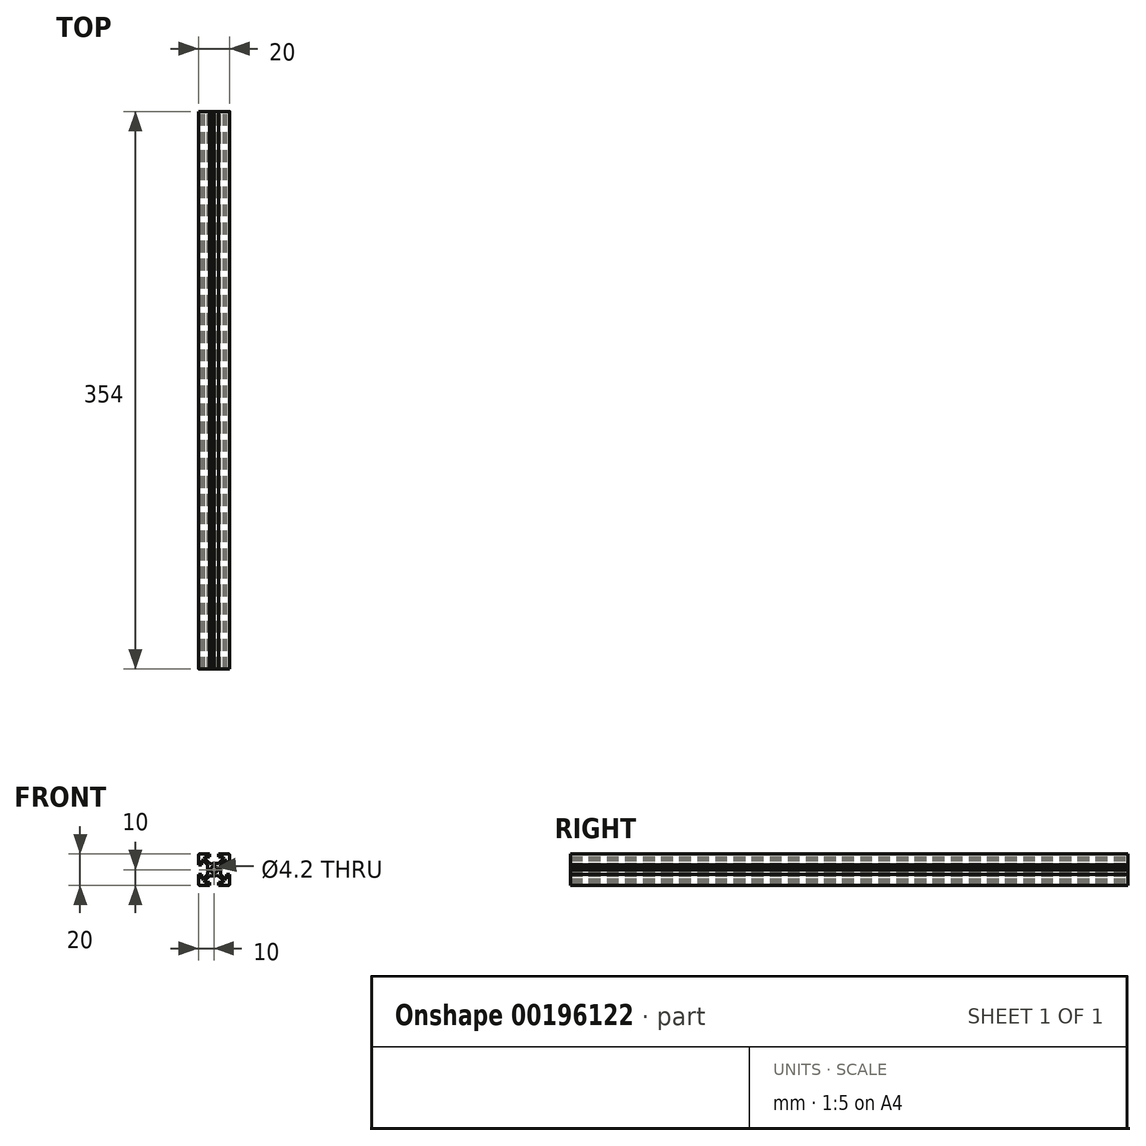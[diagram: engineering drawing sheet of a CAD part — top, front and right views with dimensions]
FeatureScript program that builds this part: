
annotation { "Feature Type Name" : "Feature", "Feature Type Description" : "" }
export const myFeature = defineFeature(function(context is Context, id is Id, definition is map)
    precondition{}
    {
        {
            var Q0;
            Q0=qCreatedBy(makeId("Front.planeOp"),FACE);
            var sketch = newSketch(context, id + "F0", { "sketchPlane" : qUnion([Q0])});
            skLineSegment(sketch, "E0.0", {"start": v(-6, -7.06) * mm, "end": v(-2.94, -4) * mm});
            skArc(sketch, "E0.1", {"start": v(-9, 10) * mm, "mid": v(-9.7, 9.7) * mm, "end": v(-10, 9) * mm});
            skLineSegment(sketch, "E0.2", {"start": v(6, 7.06) * mm, "end": v(2.94, 4) * mm});
            skLineSegment(sketch, "E0.3", {"start": v(4, 2.94) * mm, "end": v(7.06, 6) * mm});
            skCircle(sketch, "E0.4", {"center": v(0, 0) * mm, "radius": 2.1 * mm});
            skArc(sketch, "E0.5", {"start": v(9, -10) * mm, "mid": v(9.7, -9.7) * mm, "end": v(10, -9) * mm});
            skLineSegment(sketch, "E0.6", {"start": v(-4, -2.94) * mm, "end": v(-7.06, -6) * mm});
            skLineSegment(sketch, "E0.7", {"start": v(7.06, 6) * mm, "end": v(8, 6) * mm});
            skLineSegment(sketch, "E0.8", {"start": v(3, -10) * mm, "end": v(9, -10) * mm});
            skLineSegment(sketch, "E0.9", {"start": v(7.06, -6) * mm, "end": v(4, -2.94) * mm});
            skLineSegment(sketch, "E0.10", {"start": v(2.94, -4) * mm, "end": v(6, -7.06) * mm});
            skLineSegment(sketch, "E0.12", {"start": v(-3, 8) * mm, "end": v(-3, 10) * mm});
            skLineSegment(sketch, "E0.13", {"start": v(1.22, -3.75) * mm, "end": v(2.5, -4) * mm});
            skLineSegment(sketch, "E0.14", {"start": v(-9, -10) * mm, "end": v(-3, -10) * mm});
            skLineSegment(sketch, "E0.15", {"start": v(-0.9, 3.93) * mm, "end": v(-1.22, 3.75) * mm});
            skLineSegment(sketch, "E0.16", {"start": v(8, -6) * mm, "end": v(7.06, -6) * mm});
            skCircle(sketch, "E0.17", {"center": v(0, 0) * mm, "radius": 2.1 * mm});
            skLineSegment(sketch, "E0.18", {"start": v(9, 10) * mm, "end": v(3, 10) * mm});
            skLineSegment(sketch, "E0.19", {"start": v(8, -3) * mm, "end": v(8, -6) * mm});
            skLineSegment(sketch, "E0.20", {"start": v(8, 3) * mm, "end": v(10, 3) * mm});
            skLineSegment(sketch, "E0.21", {"start": v(-4, 2.94) * mm, "end": v(-4, 0.65) * mm});
            skArc(sketch, "E0.22", {"start": v(10, 9) * mm, "mid": v(9.7, 9.7) * mm, "end": v(9, 10) * mm});
            skLineSegment(sketch, "E0.23", {"start": v(-10, 9) * mm, "end": v(-10, 3) * mm});
            skLineSegment(sketch, "E0.24", {"start": v(-3.7, 0) * mm, "end": v(-3.93, -0.4) * mm});
            skLineSegment(sketch, "E0.25", {"start": v(0.4, 3.93) * mm, "end": v(0, 3.7) * mm});
            skLineSegment(sketch, "E0.26", {"start": v(-3, 10) * mm, "end": v(-9, 10) * mm});
            skLineSegment(sketch, "E0.27", {"start": v(-3.93, 0.4) * mm, "end": v(-3.7, 0) * mm});
            skLineSegment(sketch, "E0.29", {"start": v(-6, -7.06) * mm, "end": v(-2.94, -4) * mm});
            skLineSegment(sketch, "E0.30", {"start": v(-7.06, 6) * mm, "end": v(-4, 2.94) * mm});
            skArc(sketch, "E0.31", {"start": v(-9, 10) * mm, "mid": v(-9.7, 9.7) * mm, "end": v(-10, 9) * mm});
            skLineSegment(sketch, "E0.32", {"start": v(-6, 7.06) * mm, "end": v(-6, 8) * mm});
            skLineSegment(sketch, "E0.33", {"start": v(-3.93, -0.9) * mm, "end": v(-3.75, -1.22) * mm});
            skLineSegment(sketch, "E0.34", {"start": v(4, -2.94) * mm, "end": v(4, -0.65) * mm});
            skLineSegment(sketch, "E0.36", {"start": v(6, 8) * mm, "end": v(6, 7.06) * mm});
            skLineSegment(sketch, "E0.37", {"start": v(4, 2.5) * mm, "end": v(4, 2.94) * mm});
            skLineSegment(sketch, "E0.38", {"start": v(3.7, 0) * mm, "end": v(3.93, 0.4) * mm});
            skArc(sketch, "E0.39", {"start": v(-4, 0.65) * mm, "mid": v(-3.98, 0.52) * mm, "end": v(-3.93, 0.4) * mm});
            skLineSegment(sketch, "E0.40", {"start": v(3.93, 0.9) * mm, "end": v(3.75, 1.22) * mm});
            skLineSegment(sketch, "E0.41", {"start": v(2.94, 4) * mm, "end": v(0.65, 4) * mm});
            skArc(sketch, "E0.42", {"start": v(-3.93, -0.4) * mm, "mid": v(-4, -0.65) * mm, "end": v(-3.93, -0.9) * mm});
            skLineSegment(sketch, "E0.43", {"start": v(-2.94, 4) * mm, "end": v(-6, 7.06) * mm});
            skLineSegment(sketch, "E0.44", {"start": v(10, 3) * mm, "end": v(10, 9) * mm});
            skLineSegment(sketch, "E0.45", {"start": v(-3.75, -1.22) * mm, "end": v(-4, -2.5) * mm});
            skArc(sketch, "E0.46", {"start": v(3.93, 0.4) * mm, "mid": v(4, 0.65) * mm, "end": v(3.93, 0.9) * mm});
            skLineSegment(sketch, "E0.48", {"start": v(-8, -3) * mm, "end": v(-10, -3) * mm});
            skLineSegment(sketch, "E0.49", {"start": v(-10, -3) * mm, "end": v(-10, -9) * mm});
            skLineSegment(sketch, "E0.50", {"start": v(0, 3.7) * mm, "end": v(-0.4, 3.93) * mm});
            skLineSegment(sketch, "E0.51", {"start": v(6, -8) * mm, "end": v(3, -8) * mm});
            skLineSegment(sketch, "E0.52", {"start": v(-2.5, 4) * mm, "end": v(-2.94, 4) * mm});
            skLineSegment(sketch, "E0.53", {"start": v(-2.94, -4) * mm, "end": v(-0.65, -4) * mm});
            skLineSegment(sketch, "E0.54", {"start": v(-6, 8) * mm, "end": v(-3, 8) * mm});
            skLineSegment(sketch, "E0.55", {"start": v(-7.06, -6) * mm, "end": v(-8, -6) * mm});
            skLineSegment(sketch, "E0.56", {"start": v(3, 8) * mm, "end": v(6, 8) * mm});
            skLineSegment(sketch, "E0.57", {"start": v(-3, -8) * mm, "end": v(-6, -8) * mm});
            skLineSegment(sketch, "E0.58", {"start": v(8, 6) * mm, "end": v(8, 3) * mm});
            skArc(sketch, "E0.59", {"start": v(0.65, 4) * mm, "mid": v(0.52, 3.98) * mm, "end": v(0.4, 3.93) * mm});
            skLineSegment(sketch, "E0.60", {"start": v(-8, -6) * mm, "end": v(-8, -3) * mm});
            skLineSegment(sketch, "E0.61", {"start": v(2.5, -4) * mm, "end": v(2.94, -4) * mm});
            skLineSegment(sketch, "E0.62", {"start": v(-4, -2.94) * mm, "end": v(-7.06, -6) * mm});
            skLineSegment(sketch, "E0.63", {"start": v(-8, 6) * mm, "end": v(-7.06, 6) * mm});
            skArc(sketch, "E0.64", {"start": v(-0.4, 3.93) * mm, "mid": v(-0.65, 4) * mm, "end": v(-0.9, 3.93) * mm});
            skLineSegment(sketch, "E0.65", {"start": v(4, 2.94) * mm, "end": v(7.06, 6) * mm});
            skLineSegment(sketch, "E0.66", {"start": v(3, 10) * mm, "end": v(3, 8) * mm});
            skLineSegment(sketch, "E0.67", {"start": v(6, 7.06) * mm, "end": v(2.94, 4) * mm});
            skLineSegment(sketch, "E0.68", {"start": v(3.75, 1.22) * mm, "end": v(4, 2.5) * mm});
            skArc(sketch, "E0.70", {"start": v(-10, -9) * mm, "mid": v(-9.7, -9.7) * mm, "end": v(-9, -10) * mm});
            skArc(sketch, "E0.71", {"start": v(9, -10) * mm, "mid": v(9.7, -9.7) * mm, "end": v(10, -9) * mm});
            skLineSegment(sketch, "E0.72", {"start": v(-1.22, 3.75) * mm, "end": v(-2.5, 4) * mm});
            skLineSegment(sketch, "E0.73", {"start": v(-10, 3) * mm, "end": v(-8, 3) * mm});
            skLineSegment(sketch, "E0.74", {"start": v(-4, -2.5) * mm, "end": v(-4, -2.94) * mm});
            skLineSegment(sketch, "E0.79", {"start": v(3.93, -0.4) * mm, "end": v(3.7, 0) * mm});
            skLineSegment(sketch, "E0.81", {"start": v(-10, 3) * mm, "end": v(-8, 3) * mm});
            skLineSegment(sketch, "E0.82", {"start": v(-6, 8) * mm, "end": v(-3, 8) * mm});
            skLineSegment(sketch, "E0.86", {"start": v(2.5, -4) * mm, "end": v(2.94, -4) * mm});
            skLineSegment(sketch, "E0.88", {"start": v(-3.75, -1.22) * mm, "end": v(-4, -2.5) * mm});
            skLineSegment(sketch, "E0.89", {"start": v(3.75, 1.22) * mm, "end": v(4, 2.5) * mm});
            skLineSegment(sketch, "E0.90", {"start": v(-3, 8) * mm, "end": v(-3, 10) * mm});
            skLineSegment(sketch, "E0.91", {"start": v(-7.06, 6) * mm, "end": v(-4, 2.94) * mm});
            skLineSegment(sketch, "E0.93", {"start": v(8, -3) * mm, "end": v(8, -6) * mm});
            skLineSegment(sketch, "E0.100", {"start": v(-8, -6) * mm, "end": v(-8, -3) * mm});
            skLineSegment(sketch, "E0.101", {"start": v(-8, -3) * mm, "end": v(-10, -3) * mm});
            skLineSegment(sketch, "E0.102", {"start": v(0, -3.7) * mm, "end": v(0.4, -3.93) * mm});
            skLineSegment(sketch, "E0.106", {"start": v(8, -6) * mm, "end": v(7.06, -6) * mm});
            skLineSegment(sketch, "E0.109", {"start": v(2.94, 4) * mm, "end": v(0.65, 4) * mm});
            skLineSegment(sketch, "E0.110", {"start": v(10, 3) * mm, "end": v(10, 9) * mm});
            skArc(sketch, "E0.111", {"start": v(0.4, -3.93) * mm, "mid": v(0.65, -4) * mm, "end": v(0.9, -3.93) * mm});
            skLineSegment(sketch, "E0.113", {"start": v(6, 8) * mm, "end": v(6, 7.06) * mm});
            skLineSegment(sketch, "E0.114", {"start": v(-3, -8) * mm, "end": v(-6, -8) * mm});
            skLineSegment(sketch, "E0.116", {"start": v(-6, -8) * mm, "end": v(-6, -7.06) * mm});
            skLineSegment(sketch, "E0.117", {"start": v(4, -2.94) * mm, "end": v(4, -0.65) * mm});
            skArc(sketch, "E0.119", {"start": v(-10, -9) * mm, "mid": v(-9.7, -9.7) * mm, "end": v(-9, -10) * mm});
            skLineSegment(sketch, "E0.120", {"start": v(-2.5, 4) * mm, "end": v(-2.94, 4) * mm});
            skLineSegment(sketch, "E0.123", {"start": v(-10, 9) * mm, "end": v(-10, 3) * mm});
            skArc(sketch, "E0.124", {"start": v(-0.65, -4) * mm, "mid": v(-0.52, -3.98) * mm, "end": v(-0.4, -3.93) * mm});
            skLineSegment(sketch, "E0.125", {"start": v(-6, 7.06) * mm, "end": v(-6, 8) * mm});
            skLineSegment(sketch, "E0.126", {"start": v(10, -3) * mm, "end": v(8, -3) * mm});
            skLineSegment(sketch, "E0.129", {"start": v(9, 10) * mm, "end": v(3, 10) * mm});
            skLineSegment(sketch, "E0.131", {"start": v(-0.4, -3.93) * mm, "end": v(0, -3.7) * mm});
            skLineSegment(sketch, "E0.132", {"start": v(10, -9) * mm, "end": v(10, -3) * mm});
            skLineSegment(sketch, "E0.134", {"start": v(3, 8) * mm, "end": v(6, 8) * mm});
            skLineSegment(sketch, "E0.136", {"start": v(-4, 2.94) * mm, "end": v(-4, 0.65) * mm});
            skLineSegment(sketch, "E0.137", {"start": v(0, 3.7) * mm, "end": v(-0.4, 3.93) * mm});
            skArc(sketch, "E0.138", {"start": v(-3.93, -0.4) * mm, "mid": v(-4, -0.65) * mm, "end": v(-3.93, -0.9) * mm});
            skArc(sketch, "E0.140", {"start": v(4, -0.65) * mm, "mid": v(3.98, -0.52) * mm, "end": v(3.93, -0.4) * mm});
            skLineSegment(sketch, "E0.142", {"start": v(3, 10) * mm, "end": v(3, 8) * mm});
            skLineSegment(sketch, "E0.143", {"start": v(-7.06, -6) * mm, "end": v(-8, -6) * mm});
            skLineSegment(sketch, "E0.144", {"start": v(-3, -10) * mm, "end": v(-3, -8) * mm});
            skLineSegment(sketch, "E0.146", {"start": v(-3.93, 0.4) * mm, "end": v(-3.7, 0) * mm});
            skLineSegment(sketch, "E0.147", {"start": v(-8, 3) * mm, "end": v(-8, 6) * mm});
            skLineSegment(sketch, "E0.148", {"start": v(4, 2.5) * mm, "end": v(4, 2.94) * mm});
            skArc(sketch, "E0.149", {"start": v(3.93, 0.4) * mm, "mid": v(4, 0.65) * mm, "end": v(3.93, 0.9) * mm});
            skLineSegment(sketch, "E0.150", {"start": v(2.94, -4) * mm, "end": v(6, -7.06) * mm});
            skLineSegment(sketch, "E0.151", {"start": v(-10, -3) * mm, "end": v(-10, -9) * mm});
            skLineSegment(sketch, "E0.152", {"start": v(-4, -2.5) * mm, "end": v(-4, -2.94) * mm});
            skLineSegment(sketch, "E0.155", {"start": v(-9, -10) * mm, "end": v(-3, -10) * mm});
            skLineSegment(sketch, "E0.156", {"start": v(-2.94, -4) * mm, "end": v(-0.65, -4) * mm});
            skLineSegment(sketch, "E0.157", {"start": v(3, -10) * mm, "end": v(9, -10) * mm});
            skLineSegment(sketch, "E0.158", {"start": v(3, -8) * mm, "end": v(3, -10) * mm});
            skLineSegment(sketch, "E0.159", {"start": v(7.06, 6) * mm, "end": v(8, 6) * mm});
            skLineSegment(sketch, "E0.160", {"start": v(8, 6) * mm, "end": v(8, 3) * mm});
            skLineSegment(sketch, "E0.161", {"start": v(6, -8) * mm, "end": v(3, -8) * mm});
            skLineSegment(sketch, "E0.162", {"start": v(-2.94, 4) * mm, "end": v(-6, 7.06) * mm});
            skLineSegment(sketch, "E0.163", {"start": v(1.22, -3.75) * mm, "end": v(2.5, -4) * mm});
            skLineSegment(sketch, "E0.164", {"start": v(-3, 10) * mm, "end": v(-9, 10) * mm});
            skLineSegment(sketch, "E0.167", {"start": v(-1.22, 3.75) * mm, "end": v(-2.5, 4) * mm});
            skLineSegment(sketch, "E0.168", {"start": v(-8, 6) * mm, "end": v(-7.06, 6) * mm});
            skLineSegment(sketch, "E0.172", {"start": v(0.9, -3.93) * mm, "end": v(1.22, -3.75) * mm});
            skArc(sketch, "E0.173", {"start": v(0.65, 4) * mm, "mid": v(0.52, 3.98) * mm, "end": v(0.4, 3.93) * mm});
            skLineSegment(sketch, "E0.178", {"start": v(8, 3) * mm, "end": v(10, 3) * mm});
            skArc(sketch, "E0.183", {"start": v(10, 9) * mm, "mid": v(9.7, 9.7) * mm, "end": v(9, 10) * mm});
            skLineSegment(sketch, "E0.184", {"start": v(7.06, -6) * mm, "end": v(4, -2.94) * mm});
            skArc(sketch, "E0.185", {"start": v(-0.4, 3.93) * mm, "mid": v(-0.65, 4) * mm, "end": v(-0.9, 3.93) * mm});
            skLineSegment(sketch, "E0.188", {"start": v(6, -7.06) * mm, "end": v(6, -8) * mm});
            skLineSegment(sketch, "E0.190", {"start": v(-0.4, -3.93) * mm, "end": v(0, -3.7) * mm});
            skLineSegment(sketch, "E0.191", {"start": v(-3.7, 0) * mm, "end": v(-3.93, -0.4) * mm});
            skLineSegment(sketch, "E0.192", {"start": v(-8, 3) * mm, "end": v(-8, 6) * mm});
            skLineSegment(sketch, "E0.194", {"start": v(10, -9) * mm, "end": v(10, -3) * mm});
            skLineSegment(sketch, "E0.195", {"start": v(-3, -10) * mm, "end": v(-3, -8) * mm});
            skLineSegment(sketch, "E0.197", {"start": v(0.4, 3.93) * mm, "end": v(0, 3.7) * mm});
            skLineSegment(sketch, "E0.200", {"start": v(6, -7.06) * mm, "end": v(6, -8) * mm});
            skLineSegment(sketch, "E0.201", {"start": v(3.93, 0.9) * mm, "end": v(3.75, 1.22) * mm});
            skLineSegment(sketch, "E0.205", {"start": v(10, -3) * mm, "end": v(8, -3) * mm});
            skLineSegment(sketch, "E0.207", {"start": v(-6, -8) * mm, "end": v(-6, -7.06) * mm});
            skLineSegment(sketch, "E0.214", {"start": v(-3.93, -0.9) * mm, "end": v(-3.75, -1.22) * mm});
            skLineSegment(sketch, "E0.215", {"start": v(3.7, 0) * mm, "end": v(3.93, 0.4) * mm});
            skArc(sketch, "E0.218", {"start": v(-4, 0.65) * mm, "mid": v(-3.98, 0.52) * mm, "end": v(-3.93, 0.4) * mm});
            skArc(sketch, "E0.219", {"start": v(0.4, -3.93) * mm, "mid": v(0.65, -4) * mm, "end": v(0.9, -3.93) * mm});
            skLineSegment(sketch, "E0.221", {"start": v(3, -8) * mm, "end": v(3, -10) * mm});
            skLineSegment(sketch, "E0.222", {"start": v(-0.9, 3.93) * mm, "end": v(-1.22, 3.75) * mm});
            skArc(sketch, "E0.225", {"start": v(-0.65, -4) * mm, "mid": v(-0.52, -3.98) * mm, "end": v(-0.4, -3.93) * mm});
            skLineSegment(sketch, "E0.226", {"start": v(0, -3.7) * mm, "end": v(0.4, -3.93) * mm});
            skLineSegment(sketch, "E0.227", {"start": v(3.93, -0.4) * mm, "end": v(3.7, 0) * mm});
            skArc(sketch, "E0.228", {"start": v(4, -0.65) * mm, "mid": v(3.98, -0.52) * mm, "end": v(3.93, -0.4) * mm});
            skLineSegment(sketch, "E0.229", {"start": v(0.9, -3.93) * mm, "end": v(1.22, -3.75) * mm});
            skSolve(sketch);
        }
        {
            var Q0;
            Q0 = qSketchRegion(id + "F0", true);
            extrude(context, id + "F1", {"entities" : qUnion([Q0]), "endBound" : BoundingType.SYMMETRIC, "depth" : 354 * mm});
        }
    });
